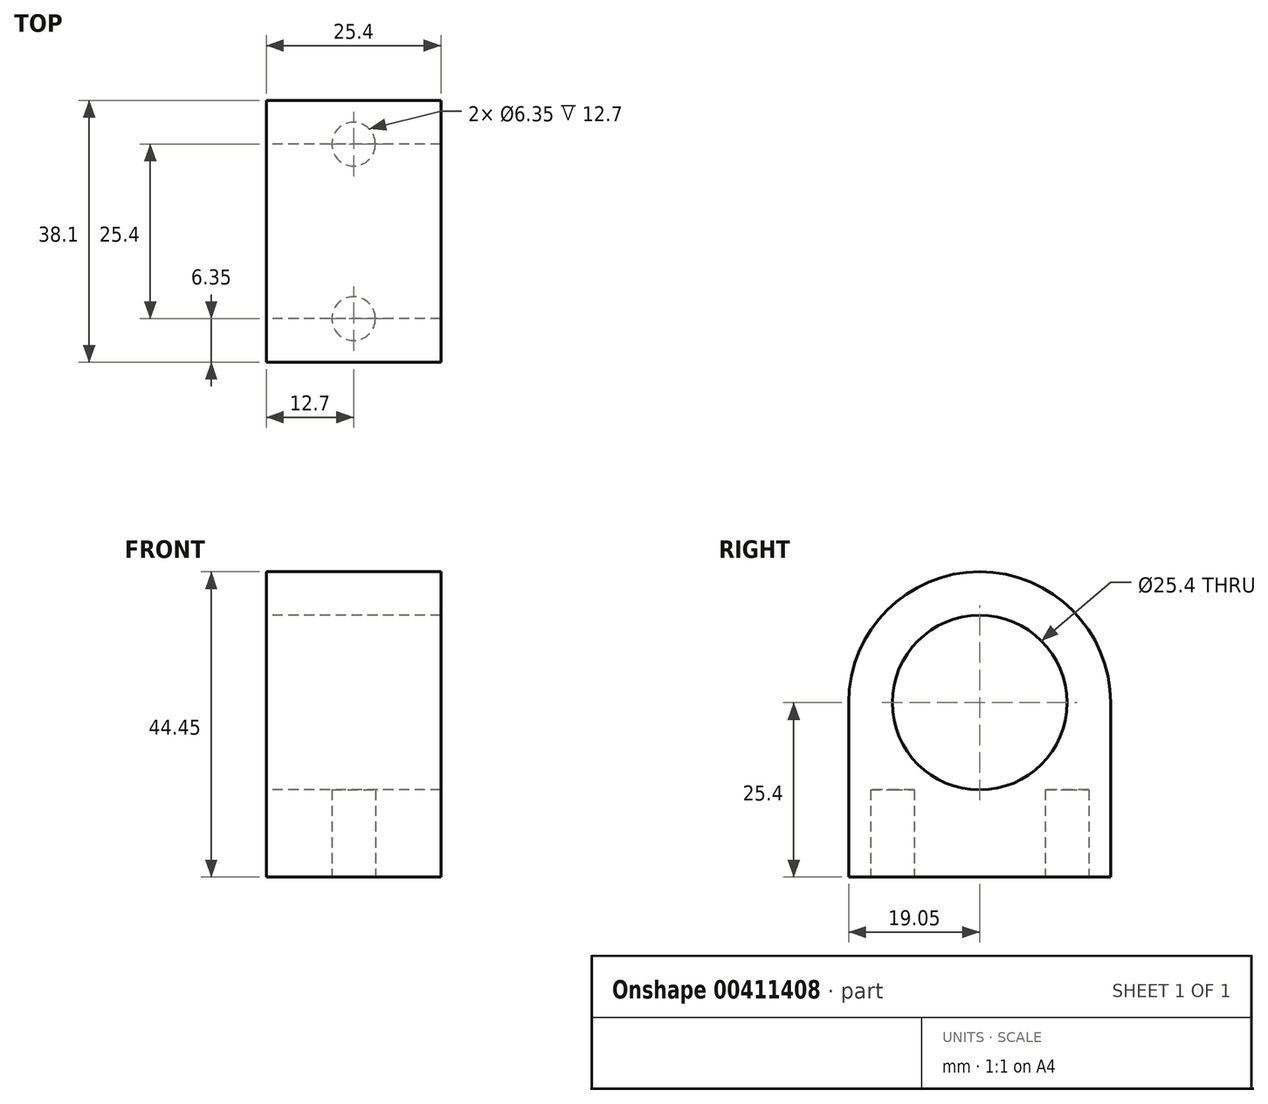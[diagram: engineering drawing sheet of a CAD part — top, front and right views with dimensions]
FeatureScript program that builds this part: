
annotation { "Feature Type Name" : "Feature", "Feature Type Description" : "" }
export const myFeature = defineFeature(function(context is Context, id is Id, definition is map)
    precondition{}
    {
        {
            var Q0;
            Q0=qCreatedBy(makeId("Right.planeOp"),FACE);
            var sketch = newSketch(context, id + "F0", { "sketchPlane" : qUnion([Q0])});
            skArc(sketch, "E0", {"start": v(19.05, 0) * mm, "mid": v(0, 19.05) * mm, "end": v(-19.05, 0) * mm});
            skLineSegment(sketch, "E1.top", {"start": v(-19.05, -25.4) * mm, "end": v(19.05, -25.4) * mm});
            skLineSegment(sketch, "E1.left", {"start": v(-19.05, 0) * mm, "end": v(-19.05, -25.4) * mm});
            skLineSegment(sketch, "E1.right", {"start": v(19.05, 0) * mm, "end": v(19.05, -25.4) * mm});
            skCircle(sketch, "E2", {"center": v(0, 0) * mm, "radius": 12.7 * mm});
            skSolve(sketch);
        }
        {
            var Q0;
            Q0 = qSketchRegion(id + "F0", true);
            extrude(context, id + "F1", {"entities" : qUnion([Q0]), "endBound" : BoundingType.SYMMETRIC, "depth" : 25.4 * mm});
        }
        {
            var Q0;
            Q0=makeQuery(id+"F1.opExtrude","SWEPT_FACE",FACE,{"disambiguationData":[OSD([sQuery(id+"F0.wireOp",EDGE,"E1.top")])]});
            var sketch = newSketch(context, id + "F2", { "sketchPlane" : qUnion([Q0])});
            skCircle(sketch, "E3", {"center": v(0, 12.7) * mm, "radius": 3.18 * mm});
            skCircle(sketch, "E4", {"center": v(0, -12.7) * mm, "radius": 3.18 * mm});
            skSolve(sketch);
        }
        {
            var Q0;
            Q0 = qSketchRegion(id + "F2", true);
            extrude(context, id + "F3", {"entities" : qUnion([Q0]), "operationType" : NewBodyOperationType.REMOVE, "oppositeDirection" : true, "depth" : 12.7 * mm});
        }
    });
